# Revit family: Wall_Hung_Lavatory_Sink-Elkay-ELV1817_3_CS3
name_source: partatom
category: Plumbing Fixtures
units: mm (PartAtom-declared; Revit-internal decimal feet)

## family parameters
Cut with Voids When Loaded = No
Host = Face
Maintain Annotation Orientation = No
OmniClass Number = 23.45.05.14.14
OmniClass Title = Sinks/Lavatories
Part Type = Normal
Room Calculation Point = No
Round Connector Dimension = Use Diameter
Shared = No

## types (2) — shared parameters
Approx. Shipping Weight (lbs) = 20
Assembly Code = D2010300
Back Splash Height = 2.5 "
Bowl 1 Dimensions = 13 5/8 inch x 10 1/8 inch x 5 13/16 inch
Bowl Depth = 5.5 "
Bowl Length = 13.63 "
Bowl Width = 10.13 "
Default Elevation = 48 "
Depth of Sink = 15.38 "
Description = Stainless Steel 18 inch x 17 1/16 inch x 5 9/16 inch Wall Hung Lavatory Sink
Drain Location = Rear Center
Drain Size = 1.5 "
Gauge = 18
Installation Type = Wall Hung
Length of Sink = 18 "
Main Material = Finish-Elkay-Stainless Steel
Manufacturer = Elkay Manufacturer Company
Manufacturer Brand = Elkay (by Zurn Elkay Water Solutions)
No of Bowls = 1
Outlet Connection Size (inch) = 1.5 "
Product Documentation Link = https://www.elkayfiles.com
Product Installation Sheet URL = https://www.elkayfiles.com
Product Page URL = https://www.elkay.com
Product Weight (lbs) = 19
Product data URL = https://www.bimobject.com
R for masking = 1.75 "
Repair Parts URL = https://www.elkayfiles.com
Sink Dimensions = 18 inch x 17 1/16 inch x 15 3/8 inch
URL = https://www.elkay.com
Width of Sink = 17.06 "
zero-valued in all types: CWFU, HWFU, WFU

## per-type parameters (varying)
| type | C/C distance of 3 Holes | Model |
| ELV1817CS3 (Wall Hung Lavatory Sink) | 4 " | ELV1817CS3 |
| ELV18173 (Wall Hung Lavatory Sink) | 8 " | ELV18173 |

## geometry (parser evidence)
native form markers: Sweep x8
no freeform markers — native parametric forms only
